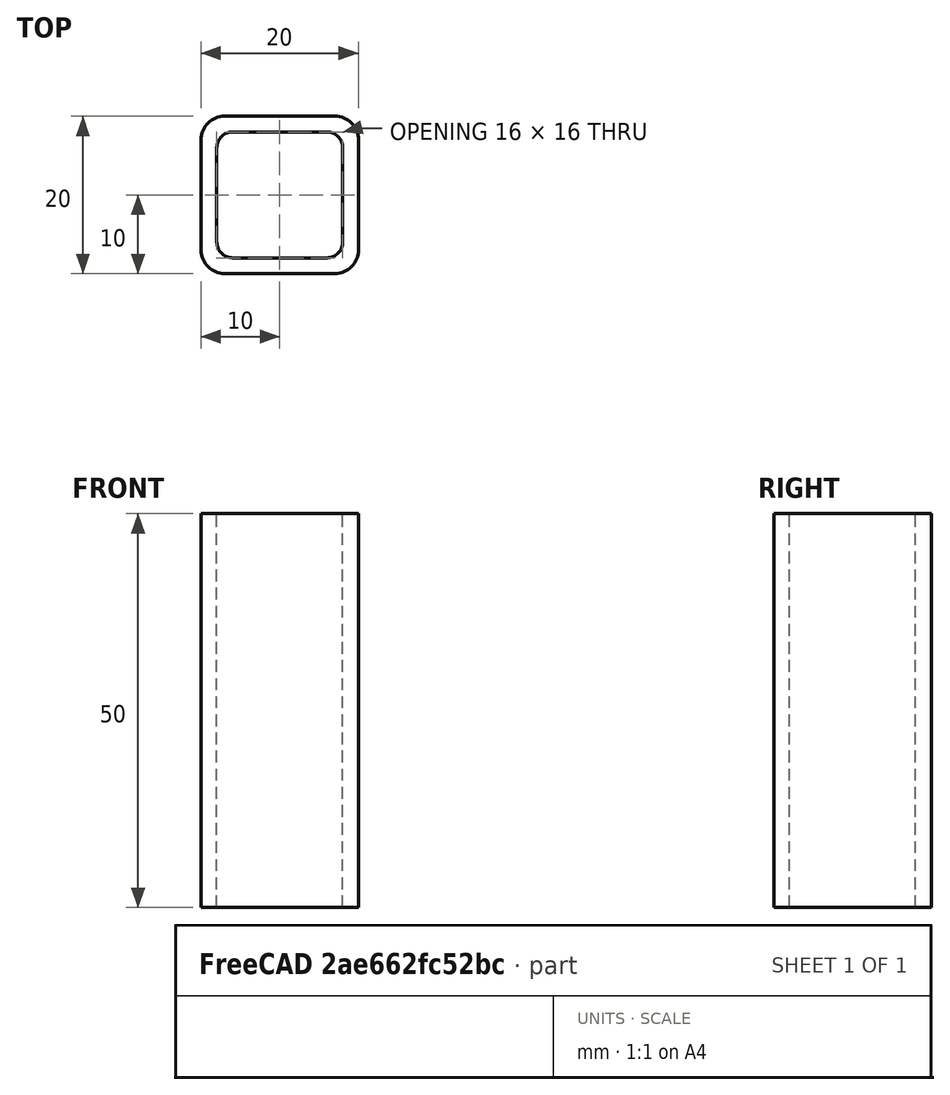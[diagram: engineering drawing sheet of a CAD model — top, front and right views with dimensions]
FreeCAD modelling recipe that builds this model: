
FCSTD DOCUMENT  (FreeCAD 0.15R4671 (Git))
Label: Square hollow section 20x20x2 EN10219 S235JRH
License: All rights reserved
LicenseURL: http://en.wikipedia.org/wiki/All_rights_reserved
objects: Sketcher::SketchObject×1, Part::Extrusion×1
note: 2 computed .brp shape members not serialized (recipe doc carries the construction recipe); baked Part::Feature solids carry a one-line shape summary decoded from their .brp

FEATURE [Sketcher::SketchObject] Sketch
  sketch-geometry (16):
    g0: LineSegment StartX=-6 StartY=8 StartZ=0 EndX=6 EndY=8 EndZ=0
    g1: LineSegment StartX=8 StartY=6 StartZ=0 EndX=8 EndY=-6 EndZ=0
    g2: LineSegment StartX=6 StartY=-8 StartZ=0 EndX=-6 EndY=-8 EndZ=0
    g3: LineSegment StartX=-8 StartY=-6 StartZ=0 EndX=-8 EndY=6 EndZ=0
    g4: LineSegment StartX=-7 StartY=10 StartZ=0 EndX=7 EndY=10 EndZ=0
    g5: LineSegment StartX=10 StartY=7 StartZ=0 EndX=10 EndY=-7 EndZ=0
    g6: LineSegment StartX=7 StartY=-10 StartZ=0 EndX=-7 EndY=-10 EndZ=0
    g7: LineSegment StartX=-10 StartY=-7 StartZ=0 EndX=-10 EndY=7 EndZ=0
    g8: ArcOfCircle CenterX=-6 CenterY=6 CenterZ=0 NormalX=0 NormalY=0 NormalZ=1 Radius=2 StartAngle=1.5708 EndAngle=3.14159
    g9: ArcOfCircle CenterX=6 CenterY=6 CenterZ=0 NormalX=0 NormalY=0 NormalZ=1 Radius=2 StartAngle=5e-12 EndAngle=1.5708
    g10: ArcOfCircle CenterX=6 CenterY=-6 CenterZ=0 NormalX=0 NormalY=0 NormalZ=1 Radius=2 StartAngle=4.71239 EndAngle=6.28319
    g11: ArcOfCircle CenterX=-6 CenterY=-6 CenterZ=0 NormalX=0 NormalY=0 NormalZ=1 Radius=2 StartAngle=3.14159 EndAngle=4.71239
    g12: ArcOfCircle CenterX=7 CenterY=7 CenterZ=0 NormalX=0 NormalY=0 NormalZ=1 Radius=3 StartAngle=0 EndAngle=1.5708
    g13: ArcOfCircle CenterX=7 CenterY=-7 CenterZ=0 NormalX=0 NormalY=0 NormalZ=1 Radius=3 StartAngle=4.71239 EndAngle=6.28319
    g14: ArcOfCircle CenterX=-7 CenterY=-7 CenterZ=0 NormalX=0 NormalY=0 NormalZ=1 Radius=3 StartAngle=3.14159 EndAngle=4.71239
    g15: ArcOfCircle CenterX=-7 CenterY=7 CenterZ=0 NormalX=0 NormalY=0 NormalZ=1 Radius=3 StartAngle=1.5708 EndAngle=3.14159
  constraints (36):
    c: Horizontal(g2)
    c: Vertical(g3)
    c: Horizontal(g6)
    c: Vertical(g7)
    c: Tangent(g3,g8) = 1.5708
    c: Tangent(g0,g8) = 1.5708
    c: Tangent(g0,g9) = 1.5708
    c: Tangent(g1,g9) = 1.5708
    c: Tangent(g1,g10) = 1.5708
    c: Tangent(g2,g10) = 1.5708
    c: Tangent(g2,g11) = 1.5708
    c: Tangent(g3,g11) = 1.5708
    c: Tangent(g4,g12) = 1.5708
    c: Tangent(g5,g12) = 1.5708
    c: Tangent(g5,g13) = 1.5708
    c: Tangent(g6,g13) = 1.5708
    c: Tangent(g6,g14) = 1.5708
    c: Tangent(g7,g14) = 1.5708
    c: Tangent(g7,g15) = 1.5708
    c: Tangent(g4,g15) = 1.5708
    c: Equal(g9,g8)
    c: Equal(g9,g11)
    c: Equal(g9,g10)
    c: Equal(g12,g15)
    c: Equal(g12,g14)
    c: Equal(g12,g13)
    c: Symmetric(g4,g6,g-1)
    c: Symmetric(g7,g5,g-2)
    c: DistanceY(g4,g6) = -20
    c: DistanceX(g7,g5) = 20
    c: Symmetric(g3,g1,g-2)
    c: Symmetric(g0,g2,g-1)
    c: DistanceY(g0,g4) = 2
    c: DistanceX(g5,g1) = -2
    c: Radius(g9) = 2
    c: Radius(g12) = 3
FEATURE [Part::Extrusion] Extrude  label="Square hollow section 20x20x2 EN10219 S235JRH"
  Base = -> Sketch
  Dir = (0,0,50)
  Solid = true
